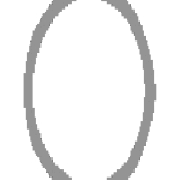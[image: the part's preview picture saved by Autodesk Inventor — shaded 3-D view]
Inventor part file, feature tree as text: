
AUTODESK INVENTOR PART (.ipt)
format: ipt  version: 2021 (Build 250183000, 183)  size: 113,664 bytes
history: native  units: in
note: dims shown in document units (in); Inventor stores cm internally (conversion verified against a paired STEP export)
features: other x4, sketch x3, plane x1
ambient origin geometry x8: Origin, YZ Plane, XZ Plane, XY Plane, X Axis, Y Axis, Z Axis, Center Point
bodies: Solid1 (feature_tree), Body (feature_tree)
feature tree (8):
  other  "Driven Length"
  other  "Frame Generator"
  other  "Start Plane"
  other  "End Plane"
  sketch  "Sketch"  dims[d2=12.0in d4=-0.0in d5=12.0in d6=0.12in d7=0.0in d8=90.0deg d9=12.0in]
  sketch  "Sketch2"  dims[d0=1.0in]
  plane  "Work Plane3"
  sketch  "Sketch3"  dims[d1=0.065in]
